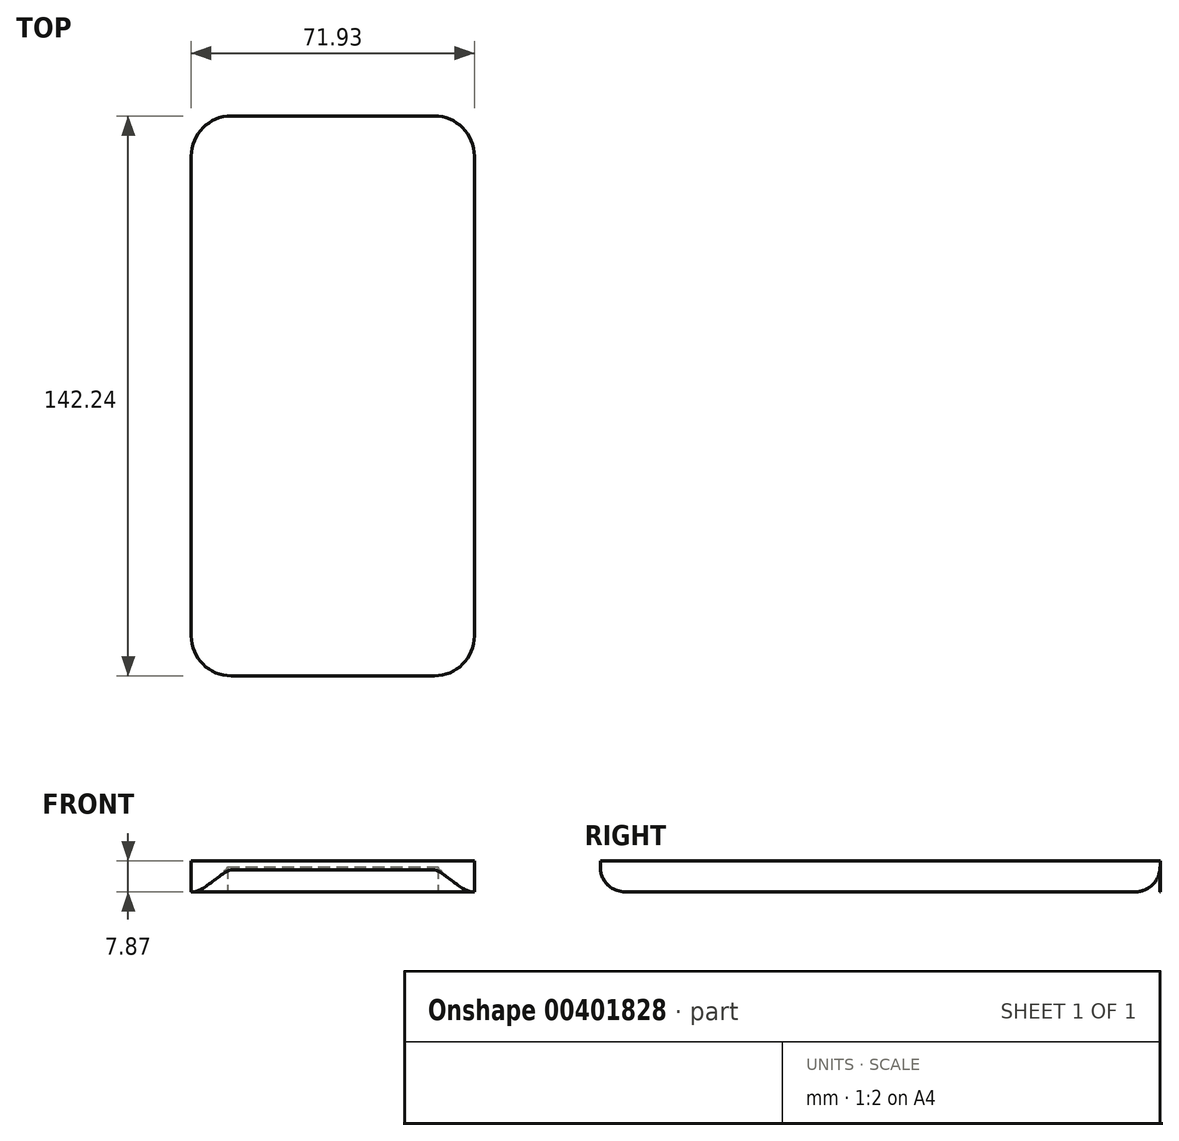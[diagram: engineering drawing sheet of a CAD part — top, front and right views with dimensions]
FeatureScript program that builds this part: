
annotation { "Feature Type Name" : "Feature", "Feature Type Description" : "" }
export const myFeature = defineFeature(function(context is Context, id is Id, definition is map)
    precondition{}
    {
        {
            var Q0;
            Q0=qCreatedBy(makeId("Top.planeOp"),FACE);
            var sketch = newSketch(context, id + "F0", { "sketchPlane" : qUnion([Q0])});
            skLineSegment(sketch, "E0", {"start": v(-44.85, -96.6) * mm, "end": v(27.08, -96.6) * mm});
            skPoint(sketch, "E1.visualSharp", {"position": v(-44.85, 45.63) * mm});
            skArc(sketch, "E1.filletArc", {"start": v(-34.69, 45.63) * mm, "mid": v(-41.87, 42.66) * mm, "end": v(-44.85, 35.47) * mm});
            skPoint(sketch, "E2.MirrorP", {"position": v(27.08, 45.63) * mm});
            skArc(sketch, "E3.MirrorCS", {"start": v(16.92, 45.63) * mm, "mid": v(24.1, 42.66) * mm, "end": v(27.08, 35.47) * mm});
            skPoint(sketch, "E4.MirrorP", {"position": v(-44.85, -96.6) * mm});
            skPoint(sketch, "E5.MirrorP", {"position": v(27.08, -96.6) * mm});
            skArc(sketch, "E6.MirrorCS", {"start": v(16.92, -96.6) * mm, "mid": v(24.1, -93.63) * mm, "end": v(27.08, -86.45) * mm});
            skArc(sketch, "E7.MirrorCS", {"start": v(-34.69, -96.6) * mm, "mid": v(-41.87, -93.63) * mm, "end": v(-44.85, -86.45) * mm});
            skLineSegment(sketch, "E8", {"start": v(-44.85, 35.47) * mm, "end": v(-44.85, -86.45) * mm});
            skLineSegment(sketch, "E9", {"start": v(-34.69, -96.6) * mm, "end": v(16.92, -96.6) * mm});
            skLineSegment(sketch, "E10", {"start": v(27.08, -86.45) * mm, "end": v(27.08, 35.47) * mm});
            skLineSegment(sketch, "E11", {"start": v(16.92, 45.63) * mm, "end": v(-34.69, 45.63) * mm});
            skLineSegment(sketch, "E12", {"start": v(27.08, -86.45) * mm, "end": v(27.08, -96.6) * mm});
            skLineSegment(sketch, "E13", {"start": v(-44.85, -86.45) * mm, "end": v(-44.85, -96.6) * mm});
            skLineSegment(sketch, "E14", {"start": v(27.08, 35.47) * mm, "end": v(27.08, 45.63) * mm});
            skLineSegment(sketch, "E15", {"start": v(27.08, 45.63) * mm, "end": v(16.92, 45.63) * mm});
            skLineSegment(sketch, "E16", {"start": v(-34.69, 45.63) * mm, "end": v(-44.85, 45.63) * mm});
            skLineSegment(sketch, "E17", {"start": v(-44.85, 35.47) * mm, "end": v(-44.85, 45.63) * mm});
            skSolve(sketch);
        }
        {
            var Q0;
            Q0=makeQuery(id+"F0.imprint","IMPRINT",FACE,{"disambiguationData":[TD([[makeQuery(id+"F0.imprint","IMPRINT",EDGE,{"derivedFrom":sQuery(id+"F0.wireOp",EDGE,"E1.filletArc")}),1.0]])]});
            extrude(context, id + "F1", {"entities" : qUnion([Q0]), "depth" : 7.87 * mm});
        }
        {
            var Q0;
            Q0=makeQuery(id+"F1.opExtrude","SWEPT_FACE",FACE,{"disambiguationData":[OSD([sQuery(id+"F0.wireOp",EDGE,"E10")])]});
            var sketch = newSketch(context, id + "F2", { "sketchPlane" : qUnion([Q0])});
            skLineSegment(sketch, "E18", {"start": v(-96.65, 7.87) * mm, "end": v(45.6, 7.87) * mm});
            skLineSegment(sketch, "E19", {"start": v(45.6, 7.87) * mm, "end": v(45.6, 0) * mm, "construction": true});
            skLineSegment(sketch, "E20", {"start": v(-25.49, 7.87) * mm, "end": v(-25.53, 0) * mm});
            skPoint(sketch, "E20.startSnap0", {"position": v(-25.49, 7.87) * mm});
            skPoint(sketch, "E20.endSnap0", {"position": v(-25.53, 7.87) * mm});
            skLineSegment(sketch, "E21", {"start": v(-25.49, 7.87) * mm, "end": v(-96.65, 7.87) * mm});
            skLineSegment(sketch, "E22", {"start": v(-25.49, 7.87) * mm, "end": v(45.6, 7.87) * mm});
            skLineSegment(sketch, "E23", {"start": v(45.6, 7.87) * mm, "end": v(45.6, 6.35) * mm});
            skLineSegment(sketch, "E24", {"start": v(39.24, 0) * mm, "end": v(-90.3, 0) * mm});
            skLineSegment(sketch, "E25", {"start": v(-96.65, 7.87) * mm, "end": v(-96.65, 6.35) * mm});
            skPoint(sketch, "E26.visualSharp", {"position": v(-96.65, 0) * mm});
            skArc(sketch, "E26.filletArc", {"start": v(-96.65, 6.35) * mm, "mid": v(-94.79, 1.86) * mm, "end": v(-90.3, 0) * mm});
            skPoint(sketch, "E27.visualSharp", {"position": v(45.6, 0) * mm});
            skArc(sketch, "E27.filletArc", {"start": v(39.24, 0) * mm, "mid": v(43.73, 1.86) * mm, "end": v(45.6, 6.35) * mm});
            skLineSegment(sketch, "E28", {"start": v(-96.65, 6.35) * mm, "end": v(-96.65, 7.87) * mm});
            skLineSegment(sketch, "E29", {"start": v(45.6, 6.35) * mm, "end": v(45.6, 0) * mm});
            skLineSegment(sketch, "E30", {"start": v(39.24, 0) * mm, "end": v(45.6, 0) * mm});
            skLineSegment(sketch, "E31", {"start": v(-96.65, 6.35) * mm, "end": v(-96.65, 0) * mm});
            skLineSegment(sketch, "E32", {"start": v(-90.3, 0) * mm, "end": v(-96.65, 0) * mm});
            skSolve(sketch);
        }
        {
            var Q0;
            Q0=makeQuery(id+"F2.imprint","IMPRINT",FACE,{"disambiguationData":[TD([[makeQuery(id+"F2.imprint","IMPRINT",EDGE,{"derivedFrom":sQuery(id+"F2.wireOp",EDGE,"E26.filletArc")}),-1.0]])]});
            var Q1;
            Q1=makeQuery(id+"F2.imprint","IMPRINT",FACE,{"disambiguationData":[TD([[makeQuery(id+"F2.imprint","IMPRINT",EDGE,{"derivedFrom":sQuery(id+"F2.wireOp",EDGE,"E27.filletArc")}),-1.0]])]});
            extrude(context, id + "F3", {"entities" : qUnion([Q0, Q1]), "operationType" : NewBodyOperationType.REMOVE, "oppositeDirection" : true, "depth" : 76.2 * mm});
        }
    });
